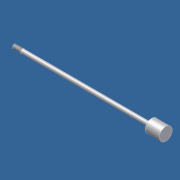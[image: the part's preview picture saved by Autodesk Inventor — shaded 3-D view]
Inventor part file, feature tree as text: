
AUTODESK INVENTOR PART (.ipt)
format: ipt  version: 2012 (Build 160160000, 160)  size: 124,928 bytes
history: native  units: in
note: dims shown in document units (in); Inventor stores cm internally (conversion verified against a paired STEP export)
features: other x84, revolve x3, sketch x3, thread x1
ambient origin geometry x8: Origin, YZ Plane, XZ Plane, XY Plane, X Axis, Y Axis, Z Axis, Center Point
bodies: Solid1 (feature_tree)
feature tree (91):
  revolve  "Revolution1"  Angle=360.0deg
  revolve  "Revolution2"  Angle=360.0deg
  thread  "Thread1"  [1 undecoded]
  revolve  "Revolution3"  [1 undecoded]
  other  "rod_cp_XY"
  other  "rod_cp_YZ"
  other  "rod_cp_ZX"
  other  "rod_cp_X"
  other  "rod_cp_Y"
  other  "rod_cp_Z"
  other  "rod_cp_Center"
  other  "to_rod_clevis_XY"
  other  "to_rod_clevis_YZ"
  other  "to_rod_clevis_ZX"
  other  "to_rod_clevis_X"
  other  "to_rod_clevis_Y"
  other  "to_rod_clevis_Z"
  other  "to_rod_clevis_Center"
  other  "rl2_XY"
  other  "rl2_YZ"
  other  "rl2_ZX"
  other  "rl2_X"
  other  "rl2_Y"
  other  "rl2_Z"
  other  "rl2_Center"
  other  "rl1_XY"
  other  "rl1_YZ"
  other  "rl1_ZX"
  other  "rl1_X"
  other  "rl1_Y"
  other  "rl1_Z"
  other  "rl1_Center"
  other  "thd1_XY"
  other  "thd1_YZ"
  other  "thd1_ZX"
  other  "thd1_X"
  other  "thd1_Y"
  other  "thd1_Z"
  other  "thd1_Center"
  other  "thd2_XY"
  other  "thd2_YZ"
  other  "thd2_ZX"
  other  "thd2_X"
  other  "thd2_Y"
  other  "thd2_Z"
  other  "thd2_Center"
  other  "dia1_XY"
  other  "dia1_YZ"
  other  "dia1_ZX"
  other  "dia1_X"
  other  "dia1_Y"
  other  "dia1_Z"
  other  "dia1_Center"
  other  "dia2_XY"
  other  "dia2_YZ"
  other  "dia2_ZX"
  other  "dia2_X"
  other  "dia2_Y"
  other  "dia2_Z"
  other  "dia2_Center"
  other  "hh1_XY"
  other  "hh1_YZ"
  other  "hh1_ZX"
  other  "hh1_X"
  other  "hh1_Y"
  other  "hh1_Z"
  other  "hh1_Center"
  other  "hh2_XY"
  other  "hh2_YZ"
  other  "hh2_ZX"
  other  "hh2_X"
  other  "hh2_Y"
  other  "hh2_Z"
  other  "hh2_Center"
  other  "dia12_XY"
  other  "dia12_YZ"
  other  "dia12_ZX"
  other  "dia12_X"
  other  "dia12_Y"
  other  "dia12_Z"
  other  "dia12_Center"
  other  "dia22_XY"
  other  "dia22_YZ"
  other  "dia22_ZX"
  other  "dia22_X"
  other  "dia22_Y"
  other  "dia22_Z"
  other  "dia22_Center"
  sketch  "Sketch_1"  dims[d0=360.0deg d1=360.0deg]
  sketch  "Sketch_3"  dims[d2=0.5in d3=7.594in d4=360.0deg]
  sketch  "Sketch_30"
note: 2 required parameter values undecoded (feature->parameter linkage not recoverable at this tier; creation-order binding heuristic only, values carry confidence <= 0.55)
